# Revit family: Seating_Inc-Kudl-Chair-Swivel
name_source: partatom
category: Furniture
revit_build: Autodesk Revit MEP 2014 (Build: 20130308_1515(x64)
units: mm (PartAtom-declared; Revit-internal decimal feet)

## types (4) — shared parameters
Assembly Code = E2020200
Depth = 26"
Height = 33 1/2"
Keynote = 12500
Leg = STI - Black
Level Pad = STI - Plastic
Manufacturer = seating inc.
Seat = STI - Fabric
Support = STI - Chrome
Type Comments = Kudl
URL = http://www.seatinginc.com
Width = 25"

## per-type parameters (varying)
| type | Description | Full Back | Model | Open Back |
| Kudl Full Back Swivel KFE20 | Kudl Full Back Swive 25"W 26"D 33.5"H | Yes | KFE20 | No |
| Kudl Open Back Swive KOE20 | Kudl Open Back Swive 25"W 26"D 33.5"H | No | KOE20 | Yes |
| Kudl Full Back Swivel Tilt KFE21 | Kudl Full Back Swivel Tilt 25"W 26"D 33.5"H | Yes | KFE21 | No |
| Kudl Open Back Swivel Tilt KOE21 | Kudl Open Back Swivel Tilt 25"W 26"D 33.5"H | No | KOE21 | Yes |

## geometry (parser evidence)
native form markers: Sweep x2
no freeform markers — native parametric forms only
